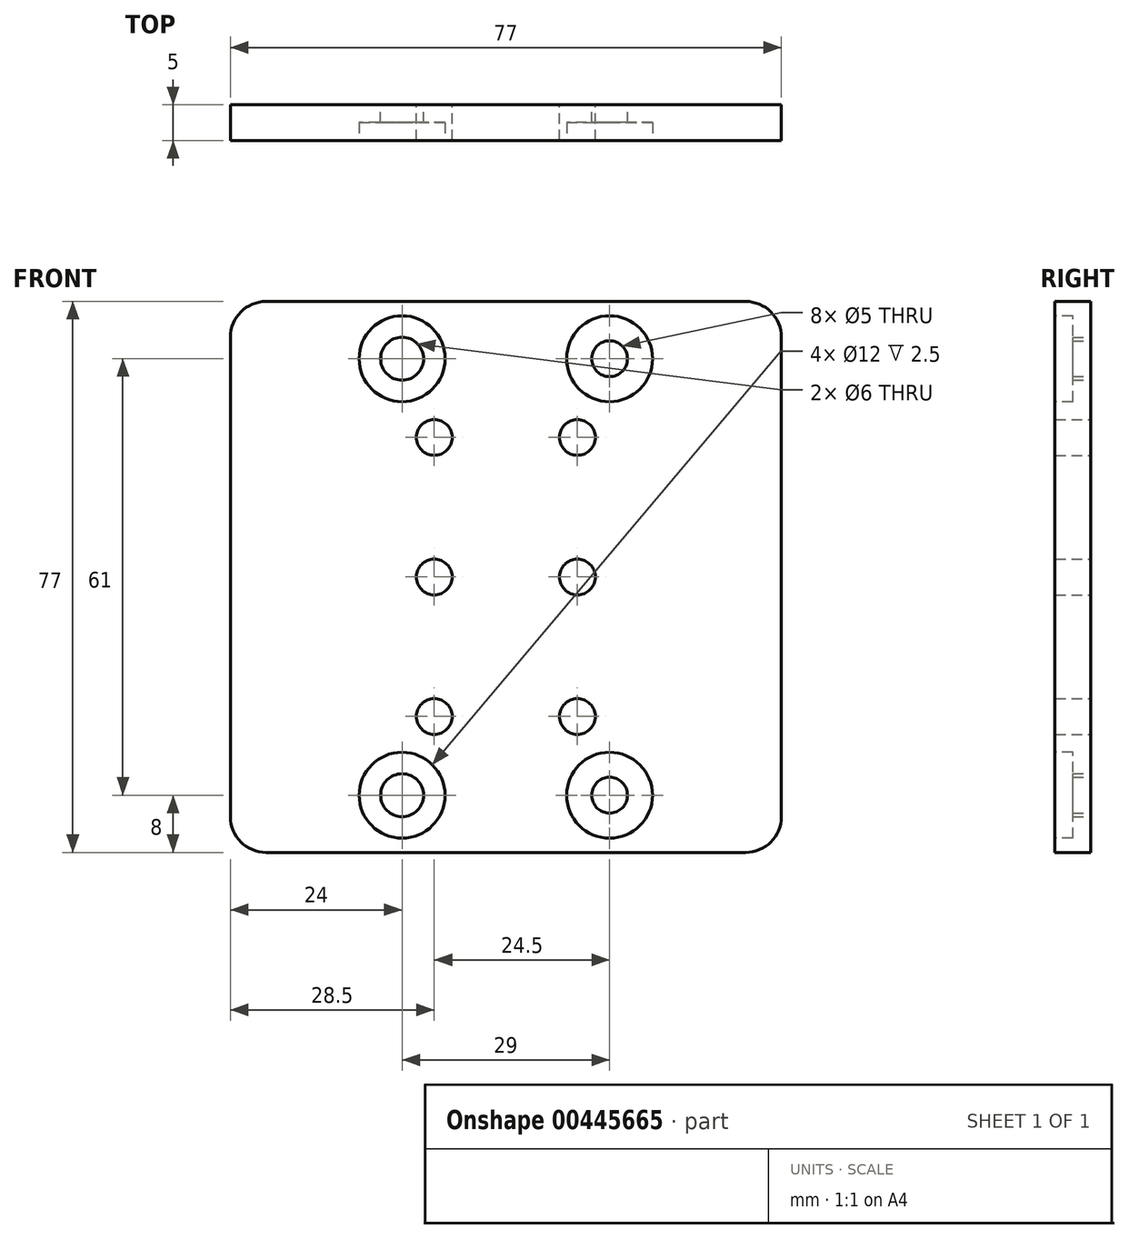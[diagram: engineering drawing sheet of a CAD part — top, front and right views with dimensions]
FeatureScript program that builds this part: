
annotation { "Feature Type Name" : "Feature", "Feature Type Description" : "" }
export const myFeature = defineFeature(function(context is Context, id is Id, definition is map)
    precondition{}
    {
        {
            var Q0;
            Q0=qCreatedBy(makeId("Front.planeOp"),FACE);
            var sketch = newSketch(context, id + "F0", { "sketchPlane" : qUnion([Q0])});
            skLineSegment(sketch, "E0.bottom", {"start": v(-33.5, -38.5) * mm, "end": v(33.5, -38.5) * mm});
            skLineSegment(sketch, "E0.top", {"start": v(-33.5, 38.5) * mm, "end": v(33.5, 38.5) * mm});
            skLineSegment(sketch, "E0.left", {"start": v(-38.5, -33.5) * mm, "end": v(-38.5, 33.5) * mm});
            skLineSegment(sketch, "E0.right", {"start": v(38.5, -33.5) * mm, "end": v(38.5, 33.5) * mm});
            skPoint(sketch, "E0.middle", {"position": v(0, 0) * mm});
            skPoint(sketch, "E1", {"position": v(-14.5, 30.5) * mm});
            skPoint(sketch, "E2", {"position": v(-10, 0) * mm});
            skPoint(sketch, "E3.MirrorP", {"position": v(-14.5, -30.5) * mm});
            skPoint(sketch, "E4.MirrorP", {"position": v(14.5, 30.5) * mm});
            skPoint(sketch, "E5.MirrorP", {"position": v(10, 0) * mm});
            skPoint(sketch, "E6.MirrorP", {"position": v(14.5, -30.5) * mm});
            skCircle(sketch, "E7", {"center": v(14.5, 30.5) * mm, "radius": 2.5 * mm});
            skCircle(sketch, "E8", {"center": v(14.5, -30.5) * mm, "radius": 2.5 * mm});
            skCircle(sketch, "E9", {"center": v(10, 0) * mm, "radius": 2.5 * mm});
            skCircle(sketch, "E10", {"center": v(-10, 0) * mm, "radius": 2.5 * mm});
            skCircle(sketch, "E11", {"center": v(-14.5, 30.5) * mm, "radius": 3 * mm});
            skCircle(sketch, "E12", {"center": v(-14.5, -30.5) * mm, "radius": 3 * mm});
            skPoint(sketch, "E13.visualSharp", {"position": v(-38.5, 38.5) * mm});
            skArc(sketch, "E13.filletArc", {"start": v(-33.5, 38.5) * mm, "mid": v(-37.04, 37.04) * mm, "end": v(-38.5, 33.5) * mm});
            skPoint(sketch, "E14.visualSharp", {"position": v(38.5, 38.5) * mm});
            skArc(sketch, "E14.filletArc", {"start": v(38.5, 33.5) * mm, "mid": v(37.04, 37.04) * mm, "end": v(33.5, 38.5) * mm});
            skPoint(sketch, "E15.visualSharp", {"position": v(38.5, -38.5) * mm});
            skArc(sketch, "E15.filletArc", {"start": v(33.5, -38.5) * mm, "mid": v(37.04, -37.04) * mm, "end": v(38.5, -33.5) * mm});
            skPoint(sketch, "E16.visualSharp", {"position": v(-38.5, -38.5) * mm});
            skArc(sketch, "E16.filletArc", {"start": v(-38.5, -33.5) * mm, "mid": v(-37.04, -37.04) * mm, "end": v(-33.5, -38.5) * mm});
            skPoint(sketch, "E17", {"position": v(-10, 19.5) * mm});
            skPoint(sketch, "E18.MirrorP", {"position": v(-10, -19.5) * mm});
            skPoint(sketch, "E19.MirrorP", {"position": v(10, 19.5) * mm});
            skPoint(sketch, "E20.MirrorP", {"position": v(10, -19.5) * mm});
            skCircle(sketch, "E21", {"center": v(-10, 19.5) * mm, "radius": 2.5 * mm});
            skCircle(sketch, "E22.MirrorC", {"center": v(-10, -19.5) * mm, "radius": 2.5 * mm});
            skCircle(sketch, "E23.MirrorC", {"center": v(10, 19.5) * mm, "radius": 2.5 * mm});
            skCircle(sketch, "E24.MirrorC", {"center": v(10, -19.5) * mm, "radius": 2.5 * mm});
            skSolve(sketch);
        }
        {
            var Q0;
            Q0=qSketchRegion(id+"F0",true);
            extrude(context, id + "F1", {"entities" : qUnion([Q0]), "depth" : 5 * mm});
        }
        {
            var Q0;
            Q0=makeQuery(id+"F1.opExtrude","CAP_FACE",FACE,{"disambiguationData":[OSD([sQuery(id+"F0.wireOp",EDGE,"E0.bottom"),sQuery(id+"F0.wireOp",EDGE,"E0.top"),sQuery(id+"F0.wireOp",EDGE,"E0.left"),sQuery(id+"F0.wireOp",EDGE,"E0.right"),sQuery(id+"F0.wireOp",EDGE,"E7"),sQuery(id+"F0.wireOp",EDGE,"E8"),sQuery(id+"F0.wireOp",EDGE,"E9"),sQuery(id+"F0.wireOp",EDGE,"E10"),sQuery(id+"F0.wireOp",EDGE,"E11"),sQuery(id+"F0.wireOp",EDGE,"E12"),sQuery(id+"F0.wireOp",EDGE,"E13.filletArc"),sQuery(id+"F0.wireOp",EDGE,"E14.filletArc"),sQuery(id+"F0.wireOp",EDGE,"E15.filletArc"),sQuery(id+"F0.wireOp",EDGE,"E16.filletArc"),sQuery(id+"F0.wireOp",EDGE,"E21"),sQuery(id+"F0.wireOp",EDGE,"E22.MirrorC"),sQuery(id+"F0.wireOp",EDGE,"E23.MirrorC"),sQuery(id+"F0.wireOp",EDGE,"E24.MirrorC")])],"isStart":false});
            var sketch = newSketch(context, id + "F2", { "sketchPlane" : qUnion([Q0])});
            skCircle(sketch, "E25", {"center": v(-14.5, 30.5) * mm, "radius": 6 * mm});
            skCircle(sketch, "E26.MirrorC", {"center": v(-14.5, -30.5) * mm, "radius": 6 * mm});
            skCircle(sketch, "E27.MirrorC", {"center": v(14.5, 30.5) * mm, "radius": 6 * mm});
            skCircle(sketch, "E28.MirrorC", {"center": v(14.5, -30.5) * mm, "radius": 6 * mm});
            skSolve(sketch);
        }
        {
            var Q0;
            Q0=qSketchRegion(id+"F2",true);
            extrude(context, id + "F3", {"entities" : qUnion([Q0]), "operationType" : NewBodyOperationType.REMOVE, "oppositeDirection" : true, "depth" : 2.5 * mm});
        }
    });
